# Revit family: ElectricalFixture_WiringAccessories_Hager_Sollysta_1Gang
name_source: partatom
category: Lighting Fixtures
revit_build: Autodesk Revit 2015 (Build: 20160512_1515(x64)
units: mm (PartAtom-declared; Revit-internal decimal feet)

## types (4) — shared parameters
CE Approval = Yes
Design Country = China
Expected Life = 25 years
Extrusion From Wall = 11.9 mm  [stored 0.039042 ft]
Frequency = 50/60Hz
Gross Weight kg = 0.165
LED Indicator Switch = No
Manufacturer = Hager
Manufacturer Country = United Kingdom
Manufacturer Website = http://www.hager.co.uk
Material = Urea Formaldehyde Thermoset Plastic
Overall Depth = 26.1 mm
Overall Height = 86 mm  [stored 0.282152 ft]
Overall Length = 86 mm  [stored 0.282152 ft]
Overall Width = 86 mm  [stored 0.282152 ft]
Packaging Recyclable = Yes
Product Family = WhiteMouldedSwitches
Product Group = WiringAccessories
Product Literature = http://www.hager.co.uk
Product Range = Sollysta
Product URL = http://www.hager.co.uk
Reference Standard = BS 1363-2
Shape = Rectangular
Shipping Weight kg = 0.188
Supply Phase = 1
Switch = Yes
Type = ElectricalFixture
Voltage (Volts) = 230V/240V

## per-type parameters (varying)
| type | Colour | Default Elevation | Description | EAN Code | Features | Finish | Name | Product Model Number | Technical Description | Unique Reference |
| WMPS11 | SollystaWhite | 1219.2 mm  [stored 4 ft] | 10AX1Gang1WayWallSwitch | 5015652260714 | 10AX1Gang1WayWallSwitch | Gloss | WhiteMouldedSwitches_WMPS11 | WMPS11 | 10AX1Gang1WayWallSwitch | WMPS11 |
| WMPS11/FAN | SollystaWhite | 1219.2 mm  [stored 4 ft] | 10AX1Gang1WayWallSwitchMarkedFan | 5015652275473 | 10AX1Gang1WayWallSwitchMarkedFan | Gloss | WhiteMouldedSwitches_WMPS11/FAN | WMPS11/FAN | 10AX1Gang1WayWallSwitchMarkedFan | WMPS11/FAN |
| WMPS12 | SollystaWhite | 1219.2 mm  [stored 4 ft] | 10AX1Gang2WayWallSwitch | 5015652260745 | 10AX1Gang2WayWallSwitch | Gloss | WhiteMouldedSwitches_WMPS12 | WMPS12 | 10AX1Gang2WayWallSwitch | WMPS12 |
| WMPS12W | RAL9010WhiteGloss | 500 mm  [stored 1.64042 ft] | 10AX1Gang2WayWallSwitchWideRocker | 5015652260745 | 10AX1Gang2WayWallSwitchWideRocker |  | WhiteMouldedSwitches_WMPS12 | WMPS12 | 10AX1Gang2WayWallSwitch | WMPS12 |

note: [stored X ft] marks values corroborated as IEEE doubles in the binary element streams (Revit-internal decimal feet)

## geometry (parser evidence)
native form markers: Blend x4, Sweep x7
no freeform markers — native parametric forms only
